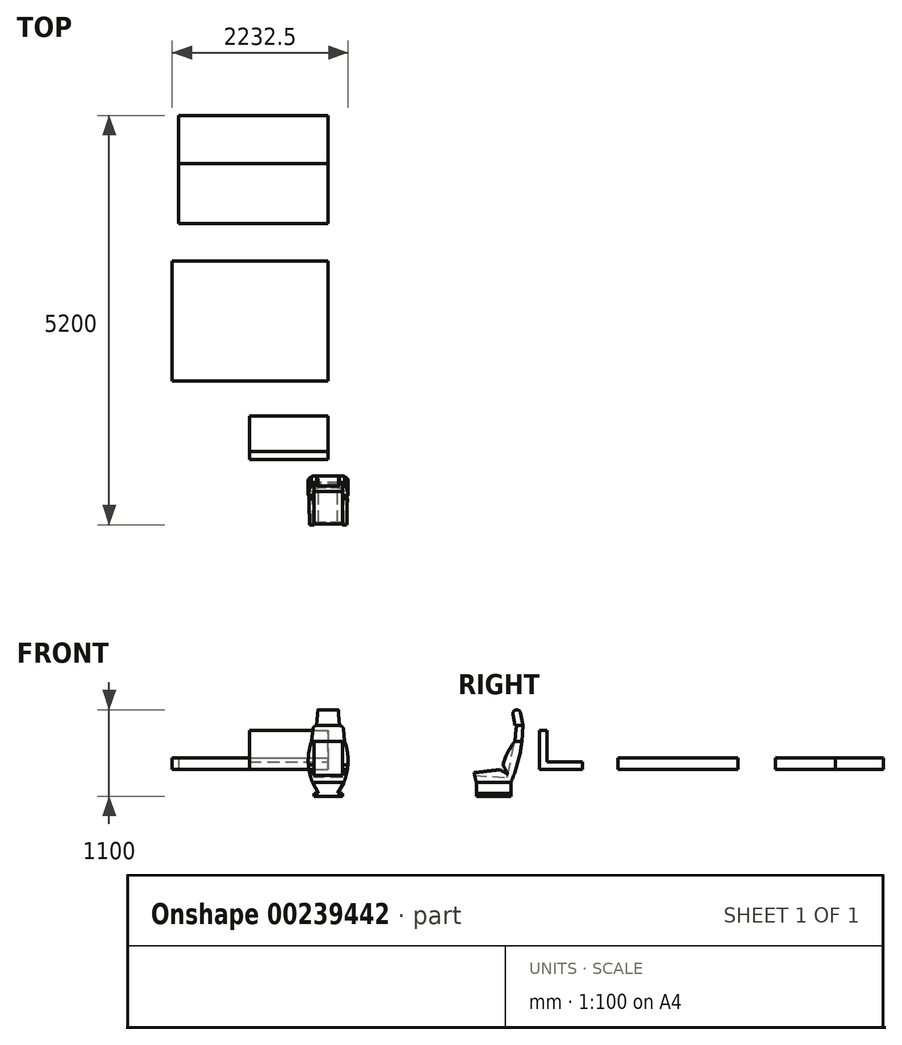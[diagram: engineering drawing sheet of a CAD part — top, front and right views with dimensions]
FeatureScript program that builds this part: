
annotation { "Feature Type Name" : "Feature", "Feature Type Description" : "" }
export const myFeature = defineFeature(function(context is Context, id is Id, definition is map)
    precondition{}
    {
        {
            var Q0;
            Q0=qCreatedBy(makeId("Front.planeOp"),FACE);
            var sketch = newSketch(context, id + "F0", { "sketchPlane" : qUnion([Q0])});
            skLineSegment(sketch, "E0.bottom", {"start": v(0, -340) * mm, "end": v(180, -340) * mm});
            skLineSegment(sketch, "E0.top", {"start": v(0, 560) * mm, "end": v(144.75, 560) * mm, "construction": true});
            skLineSegment(sketch, "E0.left", {"start": v(0, -340) * mm, "end": v(0, 560) * mm});
            skLineSegment(sketch, "E1", {"start": v(120, -300) * mm, "end": v(180, -300) * mm});
            skLineSegment(sketch, "E2", {"start": v(180, -300) * mm, "end": v(180, -340) * mm});
            skLineSegment(sketch, "E3", {"start": v(194.5, 514.98) * mm, "end": v(210, 360) * mm});
            skArc(sketch, "E4", {"start": v(200, -160) * mm, "mid": v(252.36, 99.09) * mm, "end": v(210, 360) * mm});
            skLineSegment(sketch, "E5", {"start": v(200, -160) * mm, "end": v(120, -300) * mm});
            skPoint(sketch, "E6.visualSharp", {"position": v(190, 560) * mm});
            skArc(sketch, "E6.filletArc", {"start": v(194.5, 514.98) * mm, "mid": v(178.3, 547.07) * mm, "end": v(144.75, 560) * mm});
            skLineSegment(sketch, "E7", {"start": v(0, 560) * mm, "end": v(0, 760) * mm});
            skLineSegment(sketch, "E8", {"start": v(0, 760) * mm, "end": v(130, 760) * mm});
            skLineSegment(sketch, "E9", {"start": v(130, 760) * mm, "end": v(144.75, 560) * mm});
            skSolve(sketch);
        }
        {
            var Q0;
            Q0=makeQuery(id+"F0.imprint","IMPRINT",FACE,{"disambiguationData":[TD([[makeQuery(id+"F0.imprint","IMPRINT",EDGE,{"derivedFrom":sQuery(id+"F0.wireOp",EDGE,"E0.bottom")}),1.0]])]});
            extrude(context, id + "F1", {"entities" : qUnion([Q0]), "depth" : 400 * mm, "hasSecondDirection" : true, "secondDirectionOppositeDirection" : true, "secondDirectionDepth" : 400 * mm});
        }
        {
            var Q0;
            Q0=qCreatedBy(makeId("Right.planeOp"),FACE);
            var sketch = newSketch(context, id + "F2", { "sketchPlane" : qUnion([Q0])});
            skLineSegment(sketch, "E10", {"start": v(140, -340) * mm, "end": v(-300, -340) * mm});
            skLineSegment(sketch, "E11", {"start": v(-300, -340) * mm, "end": v(-300, -160) * mm});
            skLineSegment(sketch, "E12", {"start": v(140, -160) * mm, "end": v(140, -340) * mm});
            skArc(sketch, "E13", {"start": v(140, -160) * mm, "mid": v(252.1, 192.27) * mm, "end": v(290, 560) * mm});
            skLineSegment(sketch, "E14", {"start": v(290, 560) * mm, "end": v(262.02, 718.68) * mm});
            skArc(sketch, "E15", {"start": v(262.02, 718.68) * mm, "mid": v(204.1, 759.24) * mm, "end": v(163.54, 701.32) * mm});
            skLineSegment(sketch, "E16", {"start": v(163.54, 701.32) * mm, "end": v(188.46, 560) * mm});
            skLineSegment(sketch, "E17", {"start": v(40, 60) * mm, "end": v(100, -60) * mm});
            skLineSegment(sketch, "E18", {"start": v(100, -60) * mm, "end": v(0, 0) * mm});
            skLineSegment(sketch, "E19", {"start": v(0, 0) * mm, "end": v(-330, -40) * mm});
            skLineSegment(sketch, "E20", {"start": v(-330, -40) * mm, "end": v(-300, -160) * mm});
            skLineSegment(sketch, "E21", {"start": v(188.46, 560) * mm, "end": v(210, 560) * mm});
            skLineSegment(sketch, "E22", {"start": v(210, 560) * mm, "end": v(190, 360) * mm});
            skLineSegment(sketch, "E23", {"start": v(212.78, 760) * mm, "end": v(0, 760) * mm, "construction": true});
            skArc(sketch, "E24", {"start": v(190, 360) * mm, "mid": v(99.1, 217.95) * mm, "end": v(40, 60) * mm});
            skLineSegment(sketch, "E25", {"start": v(-321.25, -75) * mm, "end": v(91.43, -100) * mm});
            skLineSegment(sketch, "E26", {"start": v(91.43, -100) * mm, "end": v(100, -60) * mm});
            skLineSegment(sketch, "E27", {"start": v(100, -60) * mm, "end": v(190, 360) * mm});
            skSolve(sketch);
        }
        {
            var Q0;
            Q0 = qSketchRegion(id + "F2", true);
            extrude(context, id + "F3", {"entities" : qUnion([Q0]), "depth" : 300 * mm});
        }
        {
            var Q0;
            Q0=makeQuery(id+"F1.opExtrude","SWEPT_BODY",BODY,{"disambiguationData":[OSD([sQuery(id+"F0.wireOp",EDGE,"E0.bottom"),sQuery(id+"F0.wireOp",EDGE,"E0.left"),sQuery(id+"F0.wireOp",EDGE,"E1"),sQuery(id+"F0.wireOp",EDGE,"E2"),sQuery(id+"F0.wireOp",EDGE,"E3"),sQuery(id+"F0.wireOp",EDGE,"E4"),sQuery(id+"F0.wireOp",EDGE,"E5"),sQuery(id+"F0.wireOp",EDGE,"E6.filletArc"),sQuery(id+"F0.wireOp",EDGE,"E7"),sQuery(id+"F0.wireOp",EDGE,"E8"),sQuery(id+"F0.wireOp",EDGE,"E9")])]});
            var Q1;
            Q1=makeQuery(id+"F3.opExtrude","SWEPT_BODY",BODY,{"disambiguationData":[OSD([sQuery(id+"F2.wireOp",EDGE,"E10"),sQuery(id+"F2.wireOp",EDGE,"E11"),sQuery(id+"F2.wireOp",EDGE,"E12"),sQuery(id+"F2.wireOp",EDGE,"E13"),sQuery(id+"F2.wireOp",EDGE,"E14"),sQuery(id+"F2.wireOp",EDGE,"E15"),sQuery(id+"F2.wireOp",EDGE,"E16"),sQuery(id+"F2.wireOp",EDGE,"E17"),sQuery(id+"F2.wireOp",EDGE,"E18"),sQuery(id+"F2.wireOp",EDGE,"E19"),sQuery(id+"F2.wireOp",EDGE,"E20"),sQuery(id+"F2.wireOp",EDGE,"E21"),sQuery(id+"F2.wireOp",EDGE,"E22"),sQuery(id+"F2.wireOp",EDGE,"E24")])]});
            booleanBodies(context, id + "F4", {"operationType" : BooleanOperationType.INTERSECTION, "tools" : qUnion([Q0, Q1])});
        }
        {
            var Q0;
            Q0=makeQuery(id+"F2.imprint","IMPRINT",FACE,{"disambiguationData":[TD([[makeQuery(id+"F2.imprint","IMPRINT",EDGE,{"derivedFrom":sQuery(id+"F2.wireOp",EDGE,"E18")}),1.0]])]});
            var Q1;
            Q1=makeQuery(id+"F2.imprint","IMPRINT",FACE,{"disambiguationData":[TD([[makeQuery(id+"F2.imprint","IMPRINT",EDGE,{"derivedFrom":sQuery(id+"F2.wireOp",EDGE,"E17")}),1.0]])]});
            extrude(context, id + "F5", {"entities" : qUnion([Q0, Q1]), "operationType" : NewBodyOperationType.REMOVE, "depth" : 180 * mm});
        }
        {
            var Q0;
            Q0=makeQuery(id+"F4.opBoolean","INTERSECT",BODY,{"derivedFrom":[makeQuery(id+"F1.opExtrude","SWEPT_BODY",BODY,{"disambiguationData":[OSD([sQuery(id+"F0.wireOp",EDGE,"E0.bottom"),sQuery(id+"F0.wireOp",EDGE,"E0.left"),sQuery(id+"F0.wireOp",EDGE,"E1"),sQuery(id+"F0.wireOp",EDGE,"E2"),sQuery(id+"F0.wireOp",EDGE,"E3"),sQuery(id+"F0.wireOp",EDGE,"E4"),sQuery(id+"F0.wireOp",EDGE,"E5"),sQuery(id+"F0.wireOp",EDGE,"E6.filletArc"),sQuery(id+"F0.wireOp",EDGE,"E7"),sQuery(id+"F0.wireOp",EDGE,"E8"),sQuery(id+"F0.wireOp",EDGE,"E9")])]}),makeQuery(id+"F3.opExtrude","SWEPT_BODY",BODY,{"disambiguationData":[OSD([sQuery(id+"F2.wireOp",EDGE,"E10"),sQuery(id+"F2.wireOp",EDGE,"E11"),sQuery(id+"F2.wireOp",EDGE,"E12"),sQuery(id+"F2.wireOp",EDGE,"E13"),sQuery(id+"F2.wireOp",EDGE,"E14"),sQuery(id+"F2.wireOp",EDGE,"E15"),sQuery(id+"F2.wireOp",EDGE,"E16"),sQuery(id+"F2.wireOp",EDGE,"E17"),sQuery(id+"F2.wireOp",EDGE,"E18"),sQuery(id+"F2.wireOp",EDGE,"E19"),sQuery(id+"F2.wireOp",EDGE,"E20"),sQuery(id+"F2.wireOp",EDGE,"E21"),sQuery(id+"F2.wireOp",EDGE,"E22"),sQuery(id+"F2.wireOp",EDGE,"E24")])]})]});
            var Q1;
            Q1=makeQuery(id+"F1.opExtrude","SWEPT_FACE",FACE,{"disambiguationData":[OSD([sQuery(id+"F0.wireOp",EDGE,"E0.left"),sQuery(id+"F0.wireOp",EDGE,"E7")])]});
            mirror(context, id + "F6", {"operationType" : NewBodyOperationType.ADD, "entities" : qUnion([Q0]), "mirrorPlane" : qUnion([Q1])});
        }
        {
            var Q0;
            Q0=qCreatedBy(makeId("Right.planeOp"),FACE);
            var sketch = newSketch(context, id + "F7", { "sketchPlane" : qUnion([Q0])});
            skLineSegment(sketch, "E28", {"start": v(600, 500) * mm, "end": v(600, 100) * mm});
            skLineSegment(sketch, "E29", {"start": v(600, 100) * mm, "end": v(1050, 100) * mm});
            skLineSegment(sketch, "E30", {"start": v(1050, 100) * mm, "end": v(1050, 0) * mm});
            skLineSegment(sketch, "E31", {"start": v(1050, 0) * mm, "end": v(500, 0) * mm});
            skLineSegment(sketch, "E32", {"start": v(500, 0) * mm, "end": v(500, 500) * mm});
            skLineSegment(sketch, "E33", {"start": v(500, 500) * mm, "end": v(600, 500) * mm});
            skLineSegment(sketch, "E34", {"start": v(500, 0) * mm, "end": v(0, 0) * mm, "construction": true});
            skSolve(sketch);
        }
        {
            var Q0;
            Q0 = qSketchRegion(id + "F7", true);
            extrude(context, id + "F8", {"entities" : qUnion([Q0]), "oppositeDirection" : true, "depth" : 1000 * mm});
        }
        {
            var Q0;
            Q0=qCreatedBy(makeId("Top.planeOp"),FACE);
            var sketch = newSketch(context, id + "F9", { "sketchPlane" : qUnion([Q0])});
            skLineSegment(sketch, "E35.bottom", {"start": v(-1980, 1500) * mm, "end": v(0, 1500) * mm});
            skLineSegment(sketch, "E35.top", {"start": v(-1980, 3020) * mm, "end": v(0, 3020) * mm});
            skLineSegment(sketch, "E35.left", {"start": v(-1980, 1500) * mm, "end": v(-1980, 3020) * mm});
            skLineSegment(sketch, "E35.right", {"start": v(0, 1500) * mm, "end": v(0, 3020) * mm});
            skLineSegment(sketch, "E36", {"start": v(0, 0) * mm, "end": v(0, 1500) * mm, "construction": true});
            skSolve(sketch);
        }
        {
            var Q0;
            Q0 = qSketchRegion(id + "F9", true);
            extrude(context, id + "F10", {"entities" : qUnion([Q0]), "depth" : 150 * mm});
        }
        {
            var Q0;
            Q0=qCreatedBy(makeId("Top.planeOp"),FACE);
            var sketch = newSketch(context, id + "F11", { "sketchPlane" : qUnion([Q0])});
            skLineSegment(sketch, "E37.bottom", {"start": v(-1900, 3500) * mm, "end": v(0, 3500) * mm});
            skLineSegment(sketch, "E37.top", {"start": v(-1900, 4260) * mm, "end": v(0, 4260) * mm});
            skLineSegment(sketch, "E37.left", {"start": v(-1900, 3500) * mm, "end": v(-1900, 4260) * mm});
            skLineSegment(sketch, "E37.right", {"start": v(0, 3500) * mm, "end": v(0, 4260) * mm});
            skLineSegment(sketch, "E38", {"start": v(0, 0) * mm, "end": v(0, 3500) * mm, "construction": true});
            skLineSegment(sketch, "E39", {"start": v(-1900, 4260) * mm, "end": v(-1900, 4870) * mm});
            skLineSegment(sketch, "E40", {"start": v(-1900, 4870) * mm, "end": v(0, 4870) * mm});
            skLineSegment(sketch, "E41", {"start": v(0, 4870) * mm, "end": v(0, 4260) * mm});
            skSolve(sketch);
        }
        {
            var Q0;
            Q0=makeQuery(id+"F11.imprint","IMPRINT",FACE,{"disambiguationData":[TD([[makeQuery(id+"F11.imprint","IMPRINT",EDGE,{"derivedFrom":sQuery(id+"F11.wireOp",EDGE,"E37.bottom")}),1.0]])]});
            extrude(context, id + "F12", {"entities" : qUnion([Q0]), "depth" : 150 * mm});
        }
        {
            var Q0;
            Q0 = qSketchRegion(id + "F11", true);
            var Q1;
            Q1=makeQuery(id+"F12.opExtrude","CAP_FACE",FACE,{"disambiguationData":[OSD([sQuery(id+"F11.wireOp",EDGE,"E37.bottom"),sQuery(id+"F11.wireOp",EDGE,"E37.top"),sQuery(id+"F11.wireOp",EDGE,"E37.left"),sQuery(id+"F11.wireOp",EDGE,"E37.right")])],"isStart":false});
            extrude(context, id + "F13", {"entities" : qUnion([Q0]), "endBound" : BoundingType.UP_TO_SURFACE, "endBoundEntityFace" : qUnion([Q1]), "depth" : 25 * mm});
        }
    });
